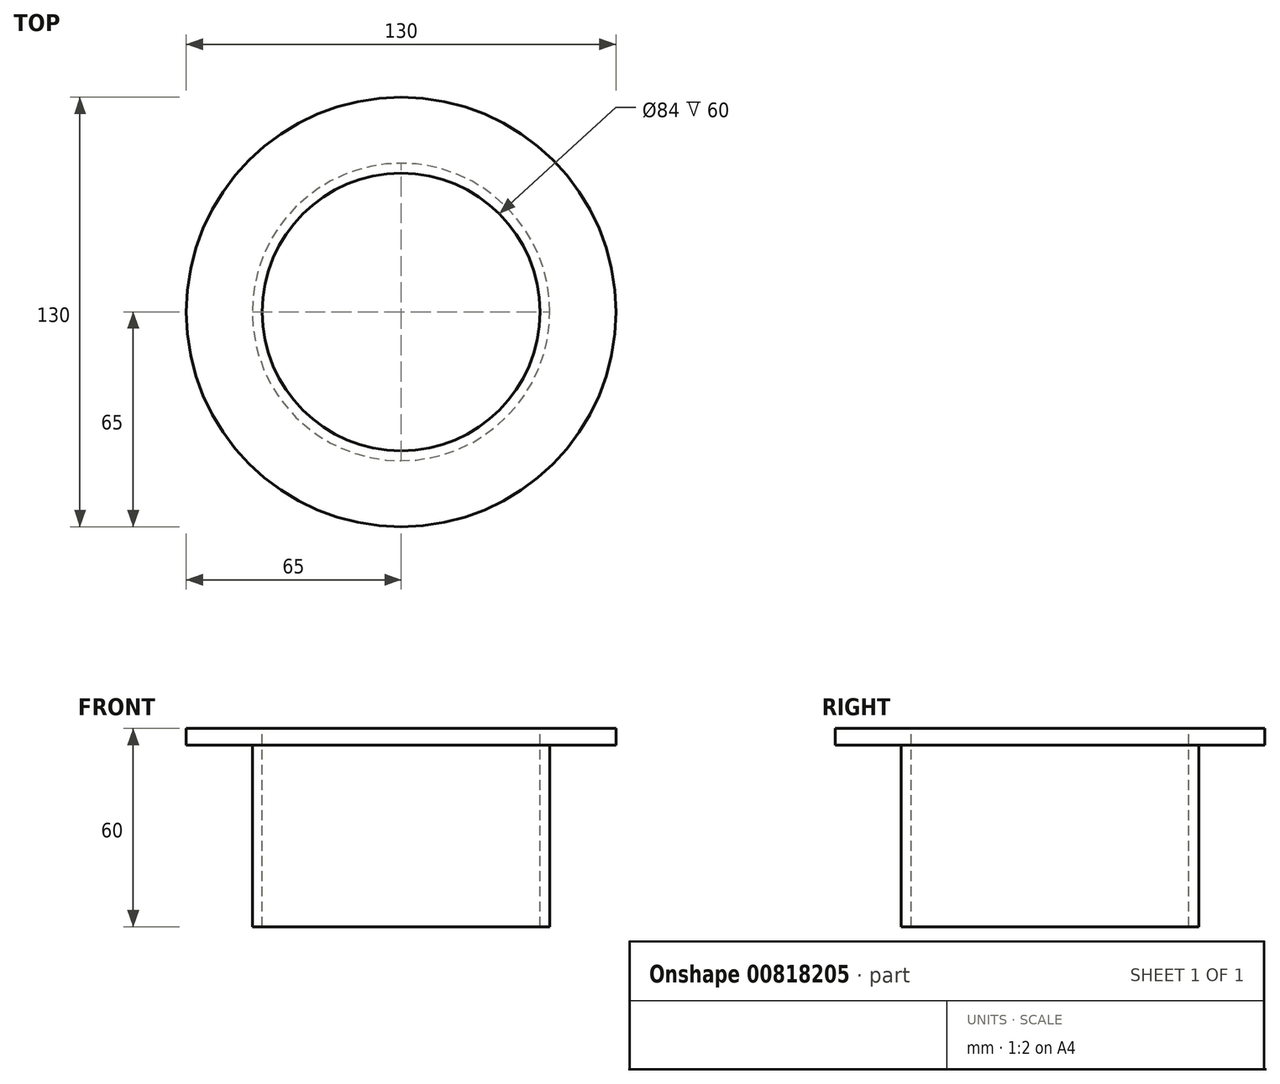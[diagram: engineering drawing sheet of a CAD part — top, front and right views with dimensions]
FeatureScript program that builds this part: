
annotation { "Feature Type Name" : "Feature", "Feature Type Description" : "" }
export const myFeature = defineFeature(function(context is Context, id is Id, definition is map)
    precondition{}
    {
        {
            var Q0;
            Q0=qCreatedBy(makeId("Front.planeOp"),FACE);
            var sketch = newSketch(context, id + "F0", { "sketchPlane" : qUnion([Q0])});
            skLineSegment(sketch, "E0", {"start": v(42, 60) * mm, "end": v(65, 60) * mm});
            skLineSegment(sketch, "E1", {"start": v(65, 60) * mm, "end": v(65, 55) * mm});
            skLineSegment(sketch, "E2", {"start": v(65, 55) * mm, "end": v(45, 55) * mm});
            skLineSegment(sketch, "E3", {"start": v(45, 55) * mm, "end": v(45, 0) * mm});
            skLineSegment(sketch, "E4", {"start": v(45, 0) * mm, "end": v(42, 0) * mm});
            skLineSegment(sketch, "E5", {"start": v(42, 0) * mm, "end": v(42, 60) * mm});
            skLineSegment(sketch, "E6", {"start": v(0, 264.77) * mm, "end": v(0, -152.68) * mm, "construction": true});
            skSolve(sketch);
        }
        {
            var Q0;
            Q0=makeQuery(id+"F0.imprint","IMPRINT",FACE,{"disambiguationData":[TD([[makeQuery(id+"F0.imprint","IMPRINT",EDGE,{"derivedFrom":sQuery(id+"F0.wireOp",EDGE,"E0")}),-1.0]])]});
            var Q1;
            Q1=sQuery(id+"F0.wireOp",EDGE,"E6");
            revolve(context, id + "F1", {"surfaceOperationType" : NewSurfaceOperationType.NEW, "entities" : qUnion([Q0]), "axis" : qUnion([Q1]), "revolveType" : RevolveType.FULL});
        }
    });
